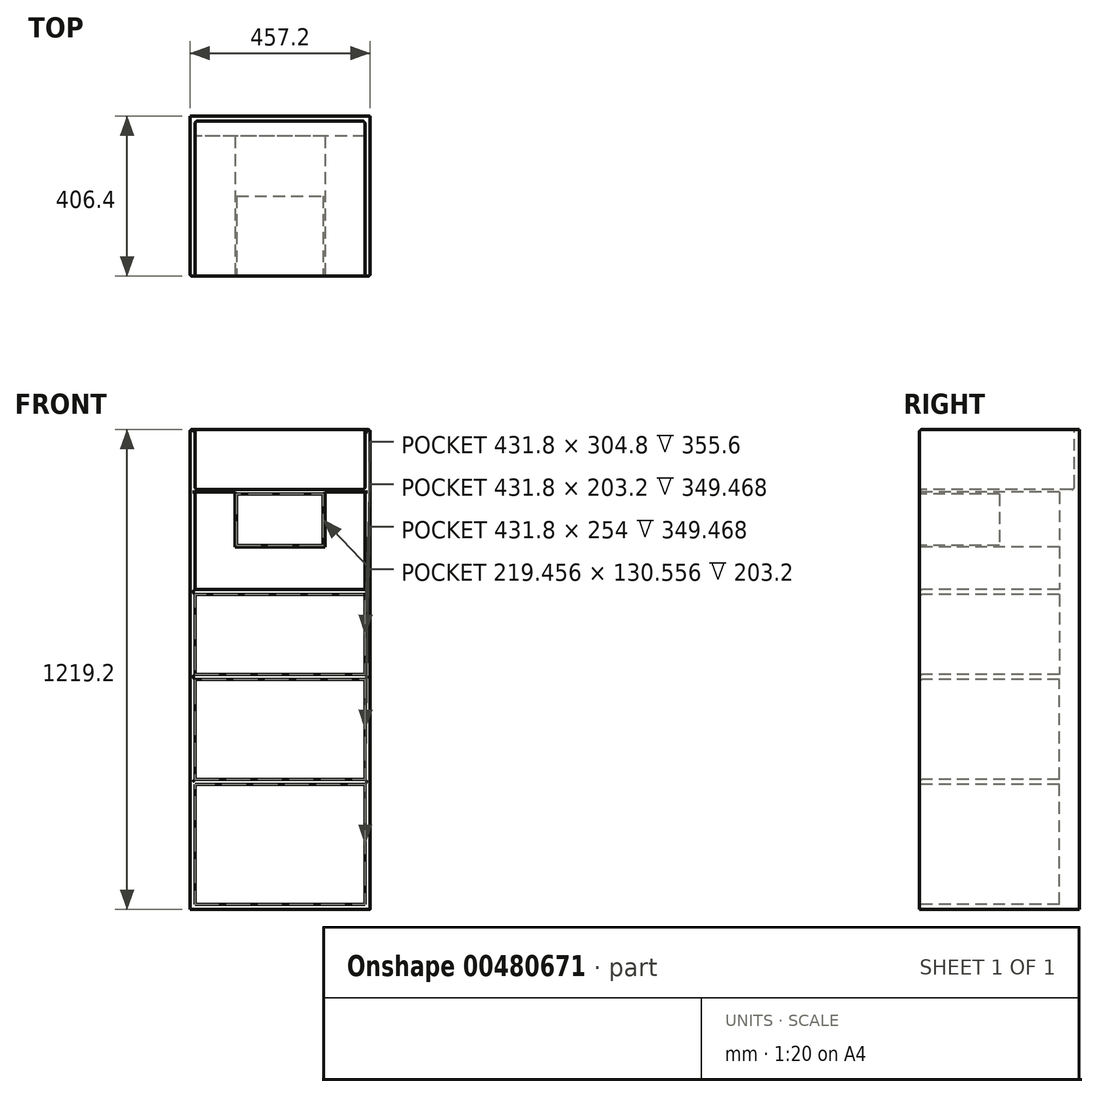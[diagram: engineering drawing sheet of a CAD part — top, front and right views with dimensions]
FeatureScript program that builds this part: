
annotation { "Feature Type Name" : "Feature", "Feature Type Description" : "" }
export const myFeature = defineFeature(function(context is Context, id is Id, definition is map)
    precondition{}
    {
        {
            var Q0;
            Q0=qCreatedBy(makeId("Top.planeOp"),FACE);
            var sketch = newSketch(context, id + "F0", { "sketchPlane" : qUnion([Q0])});
            skLineSegment(sketch, "E0.bottom", {"start": v(-235.33, 39.47) * mm, "end": v(221.87, 39.47) * mm});
            skLineSegment(sketch, "E0.top", {"start": v(-235.33, -366.93) * mm, "end": v(221.87, -366.93) * mm});
            skLineSegment(sketch, "E0.left", {"start": v(-235.33, 39.47) * mm, "end": v(-235.33, -366.93) * mm});
            skLineSegment(sketch, "E0.right", {"start": v(221.87, 39.47) * mm, "end": v(221.87, -366.93) * mm});
            skSolve(sketch);
        }
        {
            var Q0;
            Q0 = qSketchRegion(id + "F0", true);
            extrude(context, id + "F1", {"entities" : qUnion([Q0]), "oppositeDirection" : true, "depth" : 1219.2 * mm});
        }
        {
            var Q0;
            Q0=makeQuery(id+"F1.opExtrude","CAP_FACE",FACE,{"disambiguationData":[OSD([sQuery(id+"F0.wireOp",EDGE,"E0.bottom"),sQuery(id+"F0.wireOp",EDGE,"E0.top"),sQuery(id+"F0.wireOp",EDGE,"E0.left"),sQuery(id+"F0.wireOp",EDGE,"E0.right")])],"isStart":true});
            var sketch = newSketch(context, id + "F2", { "sketchPlane" : qUnion([Q0])});
            skLineSegment(sketch, "E1.bottom", {"start": v(-222.63, 26.77) * mm, "end": v(209.17, 26.77) * mm});
            skLineSegment(sketch, "E1.top", {"start": v(-222.63, -376.06) * mm, "end": v(209.17, -376.06) * mm});
            skLineSegment(sketch, "E1.left", {"start": v(-222.63, 26.77) * mm, "end": v(-222.63, -376.06) * mm});
            skLineSegment(sketch, "E1.right", {"start": v(209.17, 26.77) * mm, "end": v(209.17, -376.06) * mm});
            skSolve(sketch);
        }
        {
            var Q0;
            Q0 = qSketchRegion(id + "F2", true);
            extrude(context, id + "F3", {"entities" : qUnion([Q0]), "operationType" : NewBodyOperationType.REMOVE, "oppositeDirection" : true, "depth" : 152.4 * mm});
        }
        {
            var Q0;
            Q0=makeQuery(id+"F3.boolean.opBoolean","COPY",EDGE,{"derivedFrom":makeQuery(id+"F3.opExtrude","CAP_EDGE",EDGE,{"disambiguationData":[OSD([sQuery(id+"F2.wireOp",EDGE,"E1.right")])],"isStart":false})});
            var Q1;
            Q1=makeQuery(id+"F3.boolean.opBoolean","COPY",EDGE,{"derivedFrom":makeQuery(id+"F3.opExtrude","CAP_EDGE",EDGE,{"disambiguationData":[OSD([sQuery(id+"F2.wireOp",EDGE,"E1.bottom")])],"isStart":false})});
            var Q2;
            Q2=makeQuery(id+"F3.boolean.opBoolean","COPY",EDGE,{"derivedFrom":makeQuery(id+"F3.opExtrude","SWEPT_EDGE",EDGE,{"disambiguationData":[OSD([sQuery(id+"F2.wireOp",EDGE,"E1.bottom"),sQuery(id+"F2.wireOp",EDGE,"E1.right")])]})});
            var Q3;
            Q3=makeQuery(id+"F3.boolean.opBoolean","INTERSECT",EDGE,{"derivedFrom":[makeQuery(id+"F1.opExtrude","SWEPT_FACE",FACE,{"disambiguationData":[OSD([sQuery(id+"F0.wireOp",EDGE,"E0.top")])]}),makeQuery(id+"F3.opExtrude","SWEPT_FACE",FACE,{"disambiguationData":[OSD([sQuery(id+"F2.wireOp",EDGE,"E1.right")])]})]});
            var Q4;
            Q4=makeQuery(id+"F3.boolean.opBoolean","COPY",EDGE,{"derivedFrom":makeQuery(id+"F3.opExtrude","CAP_EDGE",EDGE,{"disambiguationData":[OSD([sQuery(id+"F2.wireOp",EDGE,"E1.right")])],"isStart":true})});
            var Q5;
            {var subQ0=sQuery(id+"F0.wireOp",EDGE,"E0.right");var subQ1=sQuery(id+"F0.wireOp",EDGE,"E0.top");Q5=makeQuery(id+"F3.boolean.opBoolean","SPLIT",EDGE,{"disambiguationData":[TD([makeQuery(id+"F1.opExtrude","SWEPT_FACE",FACE,{"disambiguationData":[OSD([subQ0])]})])],"derivedFrom":makeQuery(id+"F1.opExtrude","CAP_EDGE",EDGE,{"disambiguationData":[OSD([subQ1])],"isStart":true})});}
            var Q6;
            Q6=makeQuery(id+"F3.boolean.opBoolean","COPY",EDGE,{"derivedFrom":makeQuery(id+"F3.opExtrude","CAP_EDGE",EDGE,{"disambiguationData":[OSD([sQuery(id+"F2.wireOp",EDGE,"E1.left")])],"isStart":false})});
            var Q7;
            Q7=makeQuery(id+"F3.boolean.opBoolean","COPY",EDGE,{"derivedFrom":makeQuery(id+"F3.opExtrude","SWEPT_EDGE",EDGE,{"disambiguationData":[OSD([sQuery(id+"F2.wireOp",EDGE,"E1.bottom"),sQuery(id+"F2.wireOp",EDGE,"E1.left")])]})});
            var Q8;
            Q8=makeQuery(id+"F3.boolean.opBoolean","INTERSECT",EDGE,{"derivedFrom":[makeQuery(id+"F1.opExtrude","SWEPT_FACE",FACE,{"disambiguationData":[OSD([sQuery(id+"F0.wireOp",EDGE,"E0.top")])]}),makeQuery(id+"F3.opExtrude","CAP_FACE",FACE,{"disambiguationData":[OSD([sQuery(id+"F2.wireOp",EDGE,"E1.bottom"),sQuery(id+"F2.wireOp",EDGE,"E1.top"),sQuery(id+"F2.wireOp",EDGE,"E1.left"),sQuery(id+"F2.wireOp",EDGE,"E1.right")])],"isStart":false})]});
            var Q9;
            Q9=makeQuery(id+"F3.boolean.opBoolean","INTERSECT",EDGE,{"derivedFrom":[makeQuery(id+"F1.opExtrude","SWEPT_FACE",FACE,{"disambiguationData":[OSD([sQuery(id+"F0.wireOp",EDGE,"E0.top")])]}),makeQuery(id+"F3.opExtrude","SWEPT_FACE",FACE,{"disambiguationData":[OSD([sQuery(id+"F2.wireOp",EDGE,"E1.left")])]})]});
            var Q10;
            Q10=makeQuery(id+"F3.boolean.opBoolean","COPY",EDGE,{"derivedFrom":makeQuery(id+"F3.opExtrude","CAP_EDGE",EDGE,{"disambiguationData":[OSD([sQuery(id+"F2.wireOp",EDGE,"E1.left")])],"isStart":true})});
            var Q11;
            {var subQ0=sQuery(id+"F0.wireOp",EDGE,"E0.left");var subQ1=sQuery(id+"F0.wireOp",EDGE,"E0.top");Q11=makeQuery(id+"F3.boolean.opBoolean","SPLIT",EDGE,{"disambiguationData":[TD([makeQuery(id+"F1.opExtrude","SWEPT_FACE",FACE,{"disambiguationData":[OSD([subQ0])]})])],"derivedFrom":makeQuery(id+"F1.opExtrude","CAP_EDGE",EDGE,{"disambiguationData":[OSD([subQ1])],"isStart":true})});}
            var Q12;
            Q12=makeQuery(id+"F3.boolean.opBoolean","COPY",EDGE,{"derivedFrom":makeQuery(id+"F3.opExtrude","CAP_EDGE",EDGE,{"disambiguationData":[OSD([sQuery(id+"F2.wireOp",EDGE,"E1.bottom")])],"isStart":true})});
            fillet(context, id + "F4", {"entities" : qUnion([Q0, Q1, Q2, Q3, Q4, Q5, Q6, Q7, Q8, Q9, Q10, Q11, Q12]), "radius" : 6.76 * mm, "tangentPropagation" : true, "allowEdgeOverflow" : false});
        }
        {
            var Q0;
            Q0=makeQuery(id+"F1.opExtrude","SWEPT_FACE",FACE,{"disambiguationData":[OSD([sQuery(id+"F0.wireOp",EDGE,"E0.top")])]});
            var sketch = newSketch(context, id + "F5", { "sketchPlane" : qUnion([Q0])});
            skLineSegment(sketch, "E2.bottom", {"start": v(209.17, -1206.5) * mm, "end": v(-222.63, -1206.5) * mm});
            skLineSegment(sketch, "E2.top", {"start": v(209.17, -901.7) * mm, "end": v(-222.63, -901.7) * mm});
            skLineSegment(sketch, "E2.left", {"start": v(209.17, -1206.5) * mm, "end": v(209.17, -901.7) * mm});
            skLineSegment(sketch, "E2.right", {"start": v(-222.63, -1206.5) * mm, "end": v(-222.63, -901.7) * mm});
            skSolve(sketch);
        }
        {
            var Q0;
            Q0=makeQuery(id+"F5.imprint","IMPRINT",FACE,{"disambiguationData":[TD([[makeQuery(id+"F5.imprint","IMPRINT",EDGE,{"derivedFrom":sQuery(id+"F5.wireOp",EDGE,"E2.bottom")}),-1.0]])]});
            extrude(context, id + "F6", {"entities" : qUnion([Q0]), "operationType" : NewBodyOperationType.REMOVE, "oppositeDirection" : true, "depth" : 355.6 * mm});
        }
        {
            var Q0;
            Q0=makeQuery(id+"F1.opExtrude","SWEPT_FACE",FACE,{"disambiguationData":[OSD([sQuery(id+"F0.wireOp",EDGE,"E0.top")])]});
            var sketch = newSketch(context, id + "F7", { "sketchPlane" : qUnion([Q0])});
            skLineSegment(sketch, "E3.bottom", {"start": v(209.17, -889) * mm, "end": v(-222.63, -889) * mm});
            skLineSegment(sketch, "E3.top", {"start": v(209.17, -635) * mm, "end": v(-222.63, -635) * mm});
            skLineSegment(sketch, "E3.left", {"start": v(209.17, -889) * mm, "end": v(209.17, -635) * mm});
            skLineSegment(sketch, "E3.right", {"start": v(-222.63, -889) * mm, "end": v(-222.63, -635) * mm});
            skLineSegment(sketch, "E4.bottom", {"start": v(-222.63, -419.1) * mm, "end": v(209.17, -419.1) * mm});
            skLineSegment(sketch, "E4.top", {"start": v(-222.63, -622.3) * mm, "end": v(209.17, -622.3) * mm});
            skLineSegment(sketch, "E4.left", {"start": v(-222.63, -419.1) * mm, "end": v(-222.63, -622.3) * mm});
            skLineSegment(sketch, "E4.right", {"start": v(209.17, -419.1) * mm, "end": v(209.17, -622.3) * mm});
            skPoint(sketch, "E5.middle", {"position": v(0, -233.49) * mm});
            skLineSegment(sketch, "E6", {"start": v(-121.03, -159.16) * mm, "end": v(-222.63, -159.16) * mm});
            skLineSegment(sketch, "E7", {"start": v(-222.63, -159.16) * mm, "end": v(-222.63, -406.4) * mm});
            skLineSegment(sketch, "E8", {"start": v(-222.63, -406.4) * mm, "end": v(209.17, -406.4) * mm});
            skLineSegment(sketch, "E9", {"start": v(209.17, -406.4) * mm, "end": v(209.17, -159.16) * mm});
            skLineSegment(sketch, "E10", {"start": v(209.17, -159.16) * mm, "end": v(107.57, -159.16) * mm});
            skLineSegment(sketch, "E11", {"start": v(107.57, -159.16) * mm, "end": v(107.57, -298.86) * mm});
            skLineSegment(sketch, "E12", {"start": v(107.57, -298.86) * mm, "end": v(-121.03, -298.86) * mm});
            skLineSegment(sketch, "E13", {"start": v(-121.03, -298.86) * mm, "end": v(-121.03, -159.16) * mm});
            skSolve(sketch);
        }
        {
            var Q0;
            Q0 = qSketchRegion(id + "F7", true);
            extrude(context, id + "F8", {"entities" : qUnion([Q0]), "operationType" : NewBodyOperationType.REMOVE, "oppositeDirection" : true, "depth" : 355.6 * mm});
        }
        {
            var Q0;
            Q0=makeQuery(id+"F8.boolean.opBoolean","COPY",EDGE,{"derivedFrom":makeQuery(id+"F8.opExtrude","CAP_EDGE",EDGE,{"disambiguationData":[OSD([sQuery(id+"F7.wireOp",EDGE,"E4.left")])],"isStart":true})});
            var Q1;
            Q1=makeQuery(id+"F8.boolean.opBoolean","COPY",EDGE,{"derivedFrom":makeQuery(id+"F8.opExtrude","CAP_EDGE",EDGE,{"disambiguationData":[OSD([sQuery(id+"F7.wireOp",EDGE,"E4.right")])],"isStart":true})});
            var Q2;
            Q2=makeQuery(id+"F8.boolean.opBoolean","COPY",EDGE,{"derivedFrom":makeQuery(id+"F8.opExtrude","CAP_EDGE",EDGE,{"disambiguationData":[OSD([sQuery(id+"F7.wireOp",EDGE,"E7")])],"isStart":true})});
            var Q3;
            Q3=makeQuery(id+"F8.boolean.opBoolean","COPY",EDGE,{"derivedFrom":makeQuery(id+"F8.opExtrude","CAP_EDGE",EDGE,{"disambiguationData":[OSD([sQuery(id+"F7.wireOp",EDGE,"E9")])],"isStart":true})});
            var Q4;
            Q4=makeQuery(id+"F8.boolean.opBoolean","COPY",EDGE,{"derivedFrom":makeQuery(id+"F8.opExtrude","CAP_EDGE",EDGE,{"disambiguationData":[OSD([sQuery(id+"F7.wireOp",EDGE,"E3.left")])],"isStart":true})});
            var Q5;
            Q5=makeQuery(id+"F8.boolean.opBoolean","COPY",EDGE,{"derivedFrom":makeQuery(id+"F8.opExtrude","CAP_EDGE",EDGE,{"disambiguationData":[OSD([sQuery(id+"F7.wireOp",EDGE,"E3.right")])],"isStart":true})});
            var Q6;
            Q6=makeQuery(id+"F6.boolean.opBoolean","COPY",EDGE,{"derivedFrom":makeQuery(id+"F6.opExtrude","CAP_EDGE",EDGE,{"disambiguationData":[OSD([sQuery(id+"F5.wireOp",EDGE,"E2.right")])],"isStart":true})});
            var Q7;
            Q7=makeQuery(id+"F6.boolean.opBoolean","COPY",EDGE,{"derivedFrom":makeQuery(id+"F6.opExtrude","CAP_EDGE",EDGE,{"disambiguationData":[OSD([sQuery(id+"F5.wireOp",EDGE,"E2.left")])],"isStart":true})});
            var Q8;
            Q8=makeQuery(id+"F6.boolean.opBoolean","COPY",EDGE,{"derivedFrom":makeQuery(id+"F6.opExtrude","CAP_EDGE",EDGE,{"disambiguationData":[OSD([sQuery(id+"F5.wireOp",EDGE,"E2.bottom")])],"isStart":true})});
            var Q9;
            Q9=makeQuery(id+"F8.boolean.opBoolean","COPY",EDGE,{"derivedFrom":makeQuery(id+"F8.opExtrude","CAP_EDGE",EDGE,{"disambiguationData":[OSD([sQuery(id+"F7.wireOp",EDGE,"E3.bottom")])],"isStart":true})});
            var Q10;
            Q10=makeQuery(id+"F6.boolean.opBoolean","COPY",EDGE,{"derivedFrom":makeQuery(id+"F6.opExtrude","CAP_EDGE",EDGE,{"disambiguationData":[OSD([sQuery(id+"F5.wireOp",EDGE,"E2.top")])],"isStart":true})});
            var Q11;
            Q11=makeQuery(id+"F8.boolean.opBoolean","COPY",EDGE,{"derivedFrom":makeQuery(id+"F8.opExtrude","CAP_EDGE",EDGE,{"disambiguationData":[OSD([sQuery(id+"F7.wireOp",EDGE,"E3.top")])],"isStart":true})});
            var Q12;
            Q12=makeQuery(id+"F8.boolean.opBoolean","COPY",EDGE,{"derivedFrom":makeQuery(id+"F8.opExtrude","CAP_EDGE",EDGE,{"disambiguationData":[OSD([sQuery(id+"F7.wireOp",EDGE,"E4.top")])],"isStart":true})});
            var Q13;
            Q13=makeQuery(id+"F8.boolean.opBoolean","COPY",EDGE,{"derivedFrom":makeQuery(id+"F8.opExtrude","CAP_EDGE",EDGE,{"disambiguationData":[OSD([sQuery(id+"F7.wireOp",EDGE,"E4.bottom")])],"isStart":true})});
            var Q14;
            Q14=makeQuery(id+"F8.boolean.opBoolean","COPY",EDGE,{"derivedFrom":makeQuery(id+"F8.opExtrude","CAP_EDGE",EDGE,{"disambiguationData":[OSD([sQuery(id+"F7.wireOp",EDGE,"E8")])],"isStart":true})});
            fillet(context, id + "F9", {"entities" : qUnion([Q0, Q1, Q2, Q3, Q4, Q5, Q6, Q7, Q8, Q9, Q10, Q11, Q12, Q13, Q14]), "radius" : 6.13 * mm, "tangentPropagation" : true, "allowEdgeOverflow" : false});
        }
        {
            var Q0;
            Q0=makeQuery(id+"F5.imprint","IMPRINT",FACE,{"disambiguationData":[TD([[makeQuery(id+"F5.imprint","IMPRINT",EDGE,{"derivedFrom":sQuery(id+"F5.wireOp",EDGE,"E2.bottom")}),1.0]])]});
            var sketch = newSketch(context, id + "F10", { "sketchPlane" : qUnion([Q0])});
            skLineSegment(sketch, "E14.bottom", {"start": v(-116.46, -163.73) * mm, "end": v(103, -163.73) * mm});
            skLineSegment(sketch, "E14.top", {"start": v(-116.46, -294.28) * mm, "end": v(103, -294.28) * mm});
            skLineSegment(sketch, "E14.left", {"start": v(-116.46, -163.73) * mm, "end": v(-116.46, -294.28) * mm});
            skLineSegment(sketch, "E14.right", {"start": v(103, -163.73) * mm, "end": v(103, -294.28) * mm});
            skSolve(sketch);
        }
        {
            var Q0;
            Q0 = qSketchRegion(id + "F10", true);
            extrude(context, id + "F11", {"entities" : qUnion([Q0]), "operationType" : NewBodyOperationType.REMOVE, "oppositeDirection" : true, "depth" : 203.2 * mm});
        }
        {
            var Q0;
            {var subQ0=sQuery(id+"F0.wireOp",EDGE,"E0.right");var subQ1=makeQuery(id+"F1.opExtrude","SWEPT_FACE",FACE,{"disambiguationData":[OSD([subQ0])]});var subQ2=sQuery(id+"F0.wireOp",EDGE,"E0.top");Q0=makeQuery(id+"F4.opFillet","BLEND_EDGE",EDGE,{"blendedFrom":[makeQuery(id+"F3.boolean.opBoolean","SPLIT",EDGE,{"disambiguationData":[TD([subQ1])],"derivedFrom":makeQuery(id+"F1.opExtrude","CAP_EDGE",EDGE,{"disambiguationData":[OSD([subQ2])],"isStart":true})}),subQ1],"blendedInto":[subQ1]});}
            var Q1;
            {var subQ0=sQuery(id+"F0.wireOp",EDGE,"E0.left");var subQ1=makeQuery(id+"F1.opExtrude","SWEPT_FACE",FACE,{"disambiguationData":[OSD([subQ0])]});var subQ2=sQuery(id+"F0.wireOp",EDGE,"E0.top");Q1=makeQuery(id+"F4.opFillet","BLEND_EDGE",EDGE,{"blendedFrom":[makeQuery(id+"F3.boolean.opBoolean","SPLIT",EDGE,{"disambiguationData":[TD([subQ1])],"derivedFrom":makeQuery(id+"F1.opExtrude","CAP_EDGE",EDGE,{"disambiguationData":[OSD([subQ2])],"isStart":true})}),subQ1],"blendedInto":[subQ1]});}
            fillet(context, id + "F12", {"entities" : qUnion([Q0, Q1]), "radius" : 5.08 * mm, "tangentPropagation" : true, "allowEdgeOverflow" : false});
        }
    });
